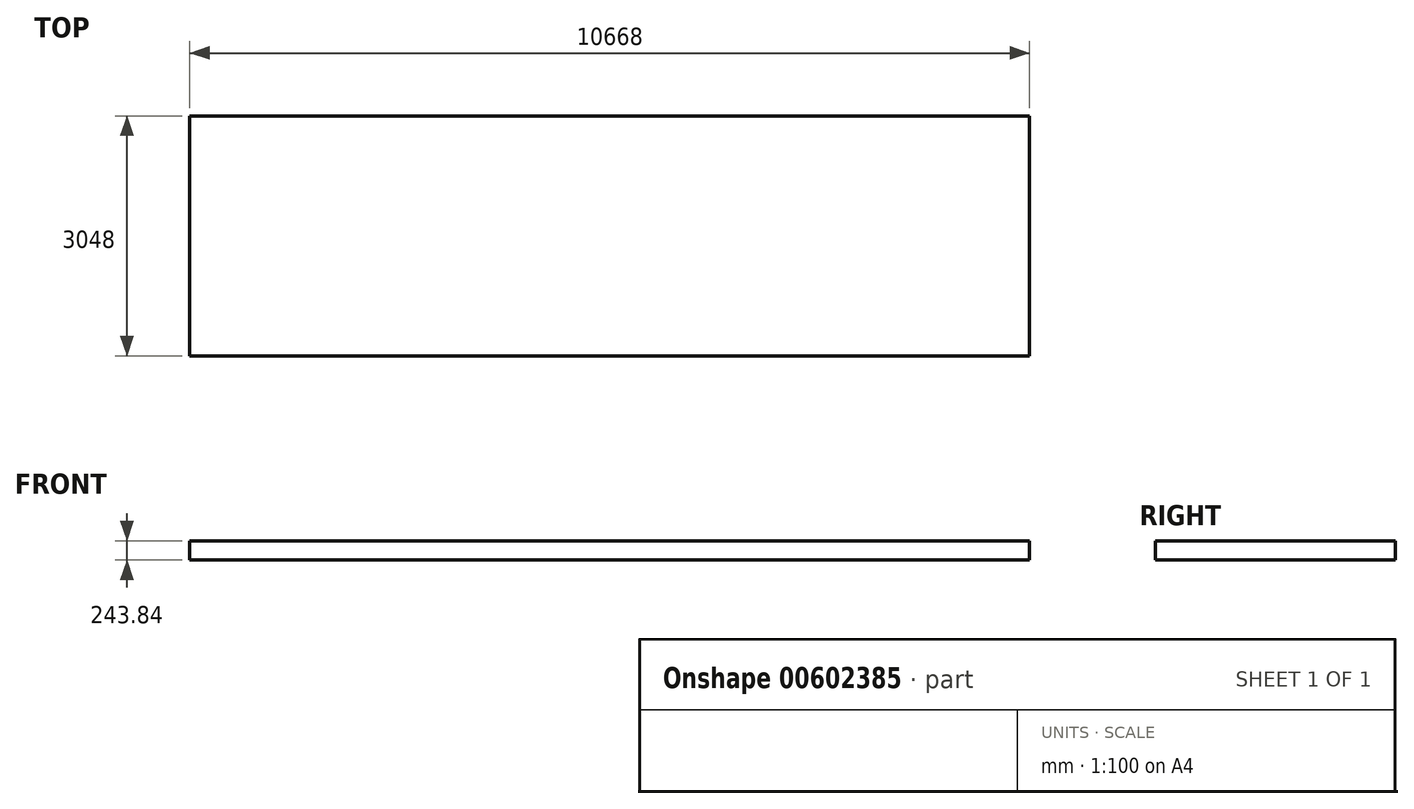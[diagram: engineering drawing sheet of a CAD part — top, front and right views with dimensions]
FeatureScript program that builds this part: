
annotation { "Feature Type Name" : "Feature", "Feature Type Description" : "" }
export const myFeature = defineFeature(function(context is Context, id is Id, definition is map)
    precondition{}
    {
        {
            var Q0;
            Q0=qCreatedBy(makeId("Top.planeOp"),FACE);
            var sketch = newSketch(context, id + "F0", { "sketchPlane" : qUnion([Q0])});
            skLineSegment(sketch, "E0.bottom", {"start": v(-5334, 1524) * mm, "end": v(5334, 1524) * mm});
            skLineSegment(sketch, "E0.top", {"start": v(-5334, -1524) * mm, "end": v(5334, -1524) * mm});
            skLineSegment(sketch, "E0.left", {"start": v(-5334, 1524) * mm, "end": v(-5334, -1524) * mm});
            skLineSegment(sketch, "E0.right", {"start": v(5334, 1524) * mm, "end": v(5334, -1524) * mm});
            skPoint(sketch, "E0.middle", {"position": v(0, 0) * mm});
            skSolve(sketch);
        }
        {
            var Q0;
            Q0=makeQuery(id+"F0.imprint","IMPRINT",FACE,{"disambiguationData":[TD([[makeQuery(id+"F0.imprint","IMPRINT",EDGE,{"derivedFrom":sQuery(id+"F0.wireOp",EDGE,"E0.bottom")}),-1.0]])]});
            extrude(context, id + "F1", {"entities" : qUnion([Q0]), "depth" : 243.84 * mm, "offsetDistance" : 30.48 * mm});
        }
    });
